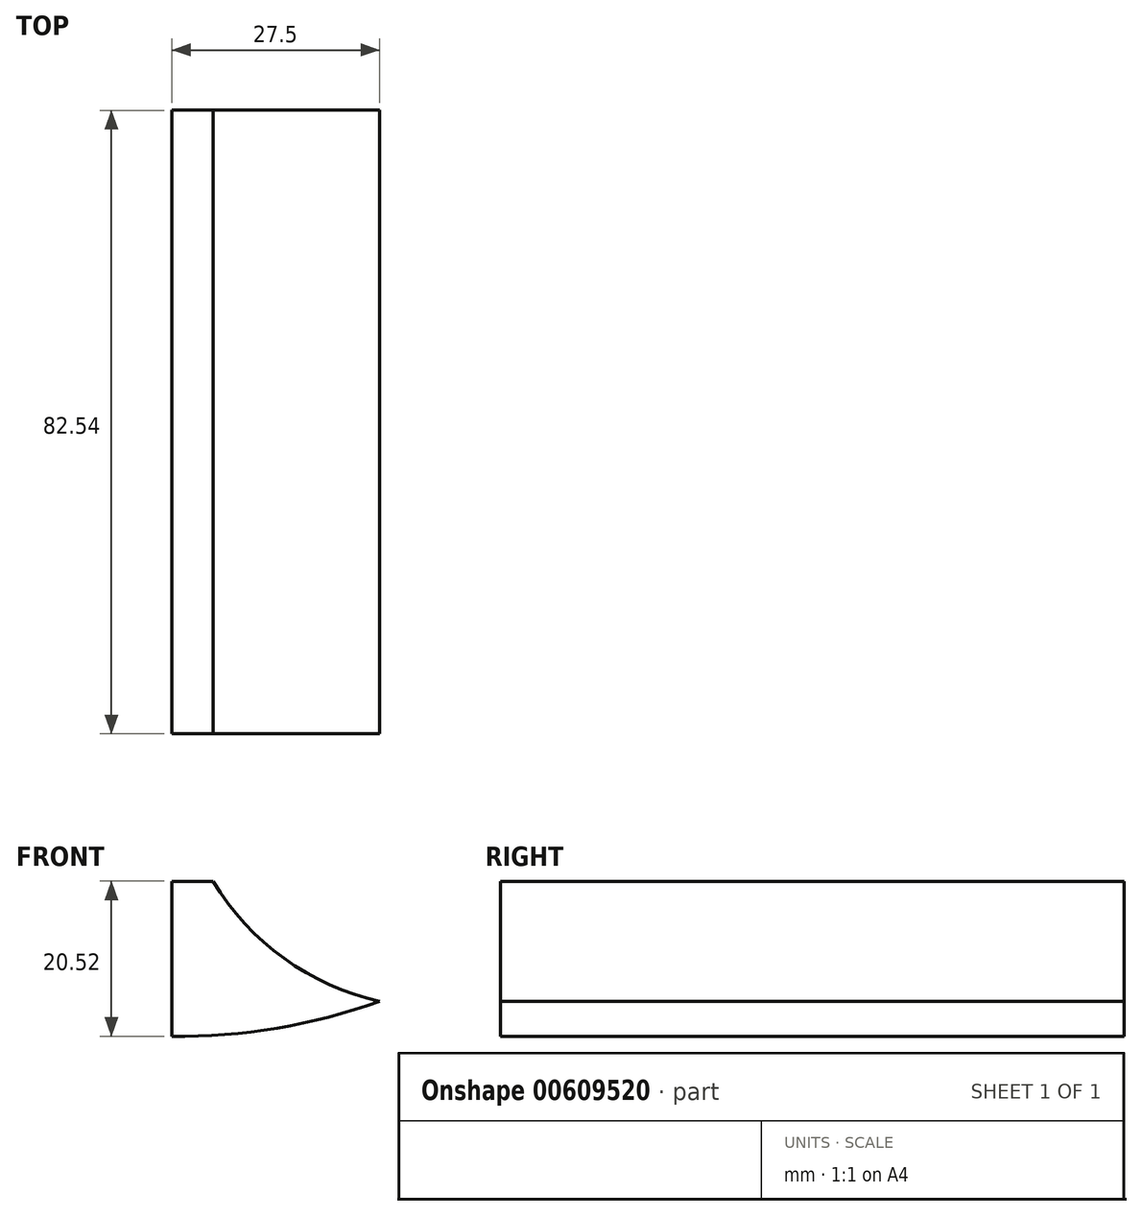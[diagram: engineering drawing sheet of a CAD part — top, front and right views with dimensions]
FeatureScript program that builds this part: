
annotation { "Feature Type Name" : "Feature", "Feature Type Description" : "" }
export const myFeature = defineFeature(function(context is Context, id is Id, definition is map)
    precondition{}
    {
        {
            var Q0;
            Q0=qCreatedBy(makeId("Front.planeOp"),FACE);
            var sketch = newSketch(context, id + "F0", { "sketchPlane" : qUnion([Q0])});
            skLineSegment(sketch, "E0.0", {"start": v(2.65, 34.25) * mm, "end": v(-16.9, 34.25) * mm});
            skLineSegment(sketch, "E0.1", {"start": v(33.9, 21.8) * mm, "end": v(33.9, 46.95) * mm});
            skLineSegment(sketch, "E0.2", {"start": v(-22.75, 21.8) * mm, "end": v(33.9, 21.8) * mm, "construction": true});
            skLineSegment(sketch, "E0.3", {"start": v(-22.75, 46.95) * mm, "end": v(-22.75, 21.8) * mm});
            skLineSegment(sketch, "E0.4", {"start": v(-16.9, 46.95) * mm, "end": v(-22.75, 46.95) * mm});
            skLineSegment(sketch, "E0.5", {"start": v(33.9, 46.95) * mm, "end": v(28.05, 46.95) * mm});
            skLineSegment(sketch, "E0.6", {"start": v(-16.9, 34.25) * mm, "end": v(-16.9, 46.95) * mm});
            skLineSegment(sketch, "E0.7", {"start": v(28.05, 46.95) * mm, "end": v(28.05, 34.25) * mm});
            skLineSegment(sketch, "E0.8", {"start": v(28.05, 34.25) * mm, "end": v(8.5, 34.25) * mm});
            skLineSegment(sketch, "E0.9", {"start": v(8.5, 34.25) * mm, "end": v(8.5, 46.95) * mm});
            skLineSegment(sketch, "E0.10", {"start": v(8.5, 46.95) * mm, "end": v(2.65, 46.95) * mm});
            skLineSegment(sketch, "E0.11", {"start": v(2.65, 46.95) * mm, "end": v(2.65, 34.25) * mm});
            skLineSegment(sketch, "E1", {"start": v(-22.75, 21.8) * mm, "end": v(-35.07, 21.8) * mm});
            skLineSegment(sketch, "E2", {"start": v(-35.07, 21.8) * mm, "end": v(-35.07, -67.1) * mm});
            skLineSegment(sketch, "E3", {"start": v(33.9, 21.8) * mm, "end": v(43.67, 21.8) * mm});
            skLineSegment(sketch, "E4", {"start": v(43.67, 21.8) * mm, "end": v(43.67, 10.53) * mm});
            skLineSegment(sketch, "E5", {"start": v(-35.07, -67.1) * mm, "end": v(-33.95, -67.1) * mm});
            skCircle(sketch, "E6", {"center": v(-0.14, -29) * mm, "radius": 31.75 * mm, "construction": true});
            skCircle(sketch, "E7", {"center": v(-0.14, -29) * mm, "radius": 5.02 * mm});
            skLineSegment(sketch, "E8", {"start": v(-35.07, -46.58) * mm, "end": v(-29.58, -46.58) * mm, "construction": true});
            skLineSegment(sketch, "E9", {"start": v(-33.95, -67.1) * mm, "end": v(-33.95, -34.7) * mm, "construction": true});
            skArc(sketch, "E10", {"start": v(-29.58, -46.58) * mm, "mid": v(32.03, -17.14) * mm, "end": v(-33.95, -34.7) * mm, "construction": true});
            skCircle(sketch, "E11", {"center": v(-28.08, -62.33) * mm, "radius": 3.18 * mm, "construction": true});
            skPoint(sketch, "E12.visualSharp", {"position": v(43.67, -67.1) * mm});
            skArc(sketch, "E12.filletArc", {"start": v(-33.95, -67.1) * mm, "mid": v(20.94, -44.36) * mm, "end": v(43.67, 10.53) * mm});
            skLineSegment(sketch, "E13", {"start": v(30.97, 9.1) * mm, "end": v(-22.37, 9.1) * mm});
            skLineSegment(sketch, "E14", {"start": v(-22.37, 9.1) * mm, "end": v(-22.37, -29) * mm});
            skArc(sketch, "E15", {"start": v(17.57, -29) * mm, "mid": v(27.31, -11.01) * mm, "end": v(30.97, 9.1) * mm});
            skArc(sketch, "E16", {"start": v(17.57, -29) * mm, "mid": v(5.5, -12.2) * mm, "end": v(-14.27, -18.3) * mm});
            skLineSegment(sketch, "E17", {"start": v(-14.27, -18.3) * mm, "end": v(-22.37, -29) * mm});
            skLineSegment(sketch, "E18", {"start": v(-0.14, -29) * mm, "end": v(-22.37, -29) * mm, "construction": true});
            skSolve(sketch);
        }
        {
            var Q0;
            Q0=qCreatedBy(makeId("Front.planeOp"),FACE);
            var sketch = newSketch(context, id + "F1", { "sketchPlane" : qUnion([Q0])});
            skLineSegment(sketch, "E19", {"start": v(-35.07, -46.58) * mm, "end": v(-29.58, -46.58) * mm});
            skLineSegment(sketch, "E20", {"start": v(-35.07, -46.58) * mm, "end": v(-35.07, -67.1) * mm});
            skArc(sketch, "E21", {"start": v(-29.58, -46.58) * mm, "mid": v(-20.21, -56.8) * mm, "end": v(-7.57, -62.47) * mm});
            skArc(sketch, "E22", {"start": v(-35.07, -67.1) * mm, "mid": v(-21.1, -66.03) * mm, "end": v(-7.57, -62.47) * mm});
            skSolve(sketch);
        }
        {
            var Q0;
            Q0 = qSketchRegion(id + "F1", true);
            extrude(context, id + "F2", {"entities" : qUnion([Q0]), "endBound" : BoundingType.SYMMETRIC, "depth" : 82.55 * mm, "offsetDistance" : 25.4 * mm});
        }
    });
